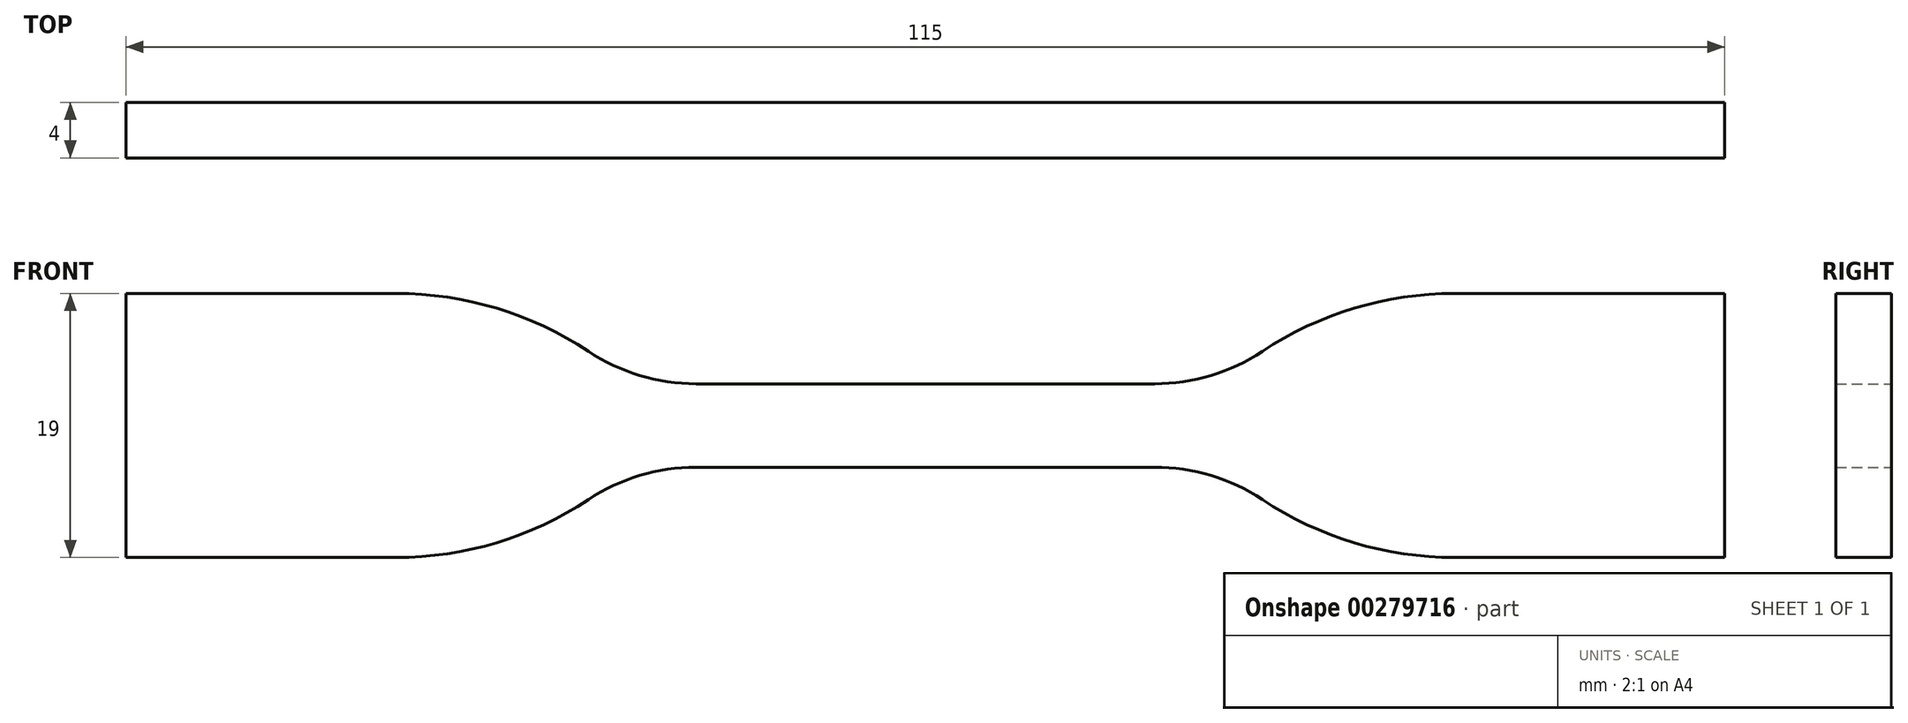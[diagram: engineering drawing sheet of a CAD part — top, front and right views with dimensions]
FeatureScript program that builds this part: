
annotation { "Feature Type Name" : "Feature", "Feature Type Description" : "" }
export const myFeature = defineFeature(function(context is Context, id is Id, definition is map)
    precondition{}
    {
        {
            var Q0;
            Q0=qCreatedBy(makeId("Front.planeOp"),FACE);
            var sketch = newSketch(context, id + "F0", { "sketchPlane" : qUnion([Q0])});
            skLineSegment(sketch, "E0", {"start": v(0, 3) * mm, "end": v(16.5, 3) * mm});
            skArc(sketch, "E1", {"start": v(16.5, 3) * mm, "mid": v(20.54, 3.6) * mm, "end": v(24.24, 5.33) * mm});
            skArc(sketch, "E2", {"start": v(24.24, 5.33) * mm, "mid": v(30.84, 8.44) * mm, "end": v(38.06, 9.5) * mm});
            skLineSegment(sketch, "E3", {"start": v(38.06, 9.5) * mm, "end": v(57.5, 9.5) * mm});
            skArc(sketch, "E4.MirrorCS", {"start": v(24.24, -5.33) * mm, "mid": v(30.84, -8.44) * mm, "end": v(38.06, -9.5) * mm});
            skLineSegment(sketch, "E5.MirrorCS", {"start": v(0, -3) * mm, "end": v(16.5, -3) * mm});
            skLineSegment(sketch, "E6.MirrorCS", {"start": v(38.06, -9.5) * mm, "end": v(57.5, -9.5) * mm});
            skArc(sketch, "E7.MirrorCS", {"start": v(16.5, -3) * mm, "mid": v(20.54, -3.6) * mm, "end": v(24.24, -5.33) * mm});
            skArc(sketch, "E8.MirrorCS", {"start": v(-16.5, 3) * mm, "mid": v(-20.54, 3.6) * mm, "end": v(-24.24, 5.33) * mm});
            skLineSegment(sketch, "E9.MirrorCS", {"start": v(0, -3) * mm, "end": v(-16.5, -3) * mm});
            skLineSegment(sketch, "E10.MirrorCS", {"start": v(-38.06, 9.5) * mm, "end": v(-57.5, 9.5) * mm});
            skLineSegment(sketch, "E11.MirrorCS", {"start": v(0, 3) * mm, "end": v(-16.5, 3) * mm});
            skLineSegment(sketch, "E12.MirrorCS", {"start": v(-38.06, -9.5) * mm, "end": v(-57.5, -9.5) * mm});
            skArc(sketch, "E13.MirrorCS", {"start": v(-24.24, -5.33) * mm, "mid": v(-30.84, -8.44) * mm, "end": v(-38.06, -9.5) * mm});
            skArc(sketch, "E14.MirrorCS", {"start": v(-24.24, 5.33) * mm, "mid": v(-30.84, 8.44) * mm, "end": v(-38.06, 9.5) * mm});
            skArc(sketch, "E15.MirrorCS", {"start": v(-16.5, -3) * mm, "mid": v(-20.54, -3.6) * mm, "end": v(-24.24, -5.33) * mm});
            skLineSegment(sketch, "E16", {"start": v(57.5, -9.5) * mm, "end": v(57.5, 9.5) * mm});
            skLineSegment(sketch, "E17", {"start": v(-57.5, -9.5) * mm, "end": v(-57.5, 9.5) * mm});
            skSolve(sketch);
        }
        {
            var Q0;
            Q0=makeQuery(id+"F0.imprint","IMPRINT",FACE,{"disambiguationData":[TD([[makeQuery(id+"F0.imprint","IMPRINT",EDGE,{"derivedFrom":sQuery(id+"F0.wireOp",EDGE,"E0")}),-1.0]])]});
            extrude(context, id + "F1", {"entities" : qUnion([Q0]), "endBound" : BoundingType.SYMMETRIC, "depth" : 4 * mm});
        }
    });
